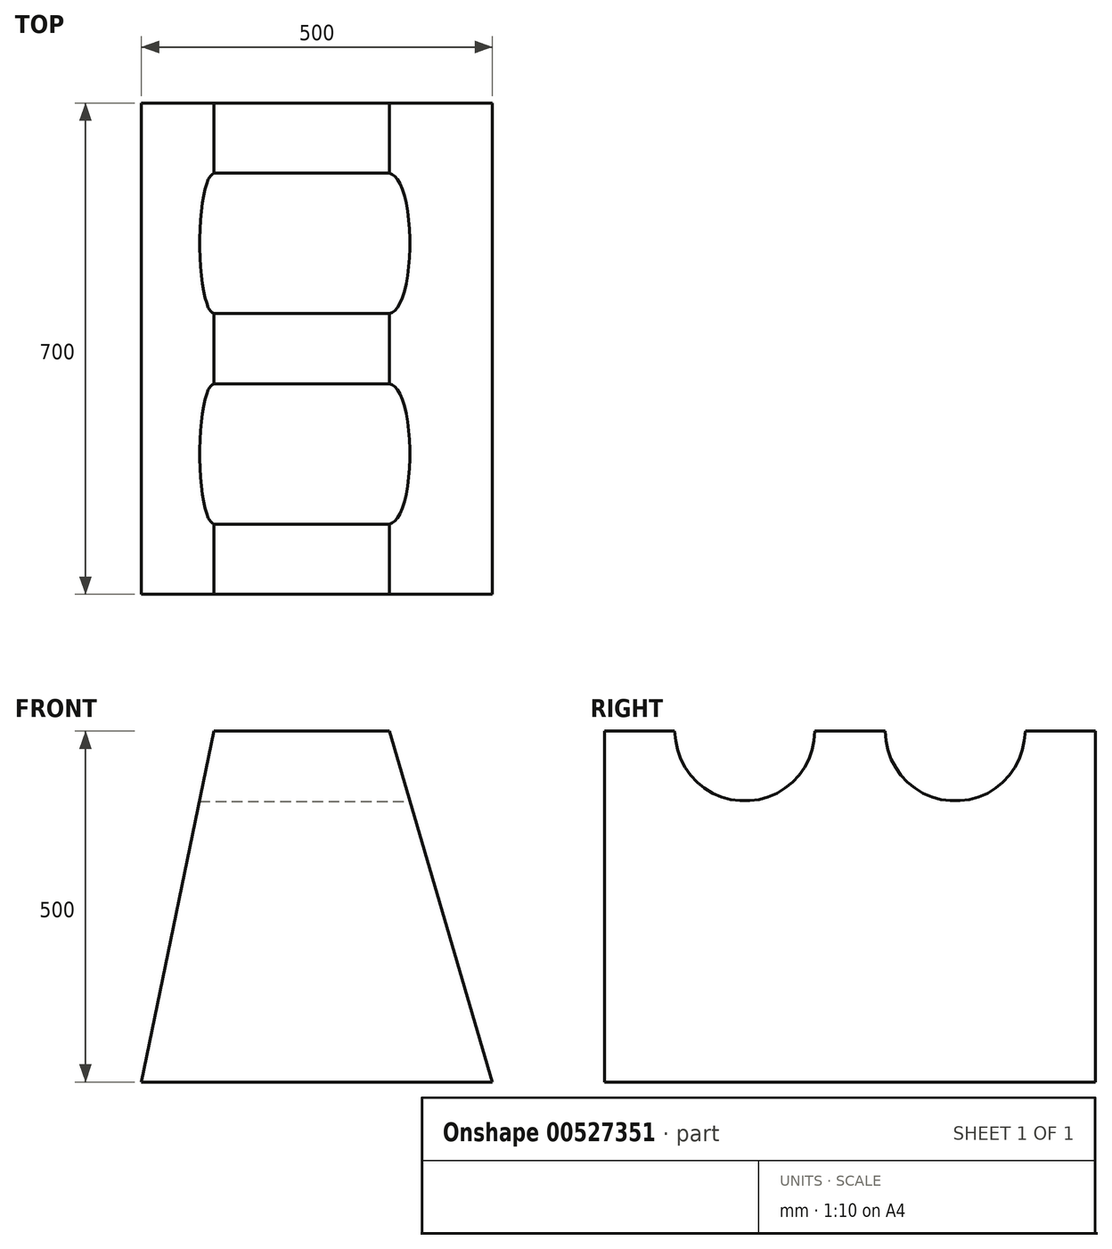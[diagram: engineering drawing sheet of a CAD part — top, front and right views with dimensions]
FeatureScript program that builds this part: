
annotation { "Feature Type Name" : "Feature", "Feature Type Description" : "" }
export const myFeature = defineFeature(function(context is Context, id is Id, definition is map)
    precondition{}
    {
        {
            var Q0;
            Q0=qCreatedBy(makeId("Front.planeOp"),FACE);
            var sketch = newSketch(context, id + "F0", { "sketchPlane" : qUnion([Q0])});
            skLineSegment(sketch, "E0", {"start": v(124.12, 332.38) * mm, "end": v(-125.88, 332.38) * mm});
            skLineSegment(sketch, "E1", {"start": v(-125.88, 332.38) * mm, "end": v(-229.3, -167.62) * mm});
            skLineSegment(sketch, "E2", {"start": v(-229.3, -167.62) * mm, "end": v(270.7, -167.62) * mm});
            skLineSegment(sketch, "E3", {"start": v(270.7, -167.62) * mm, "end": v(124.12, 332.38) * mm});
            skSolve(sketch);
        }
        {
            var Q0;
            Q0 = qSketchRegion(id + "F0", true);
            extrude(context, id + "F1", {"entities" : qUnion([Q0]), "oppositeDirection" : true, "depth" : 700 * mm, "offsetDistance" : 25 * mm});
        }
        {
            var Q0;
            Q0=qCreatedBy(makeId("Right.planeOp"),FACE);
            var sketch = newSketch(context, id + "F2", { "sketchPlane" : qUnion([Q0])});
            skCircle(sketch, "E4", {"center": v(200, 332.38) * mm, "radius": 100 * mm});
            skCircle(sketch, "E5", {"center": v(500, 332.38) * mm, "radius": 100 * mm});
            skSolve(sketch);
        }
        {
            var Q0;
            Q0 = qSketchRegion(id + "F2", true);
            extrude(context, id + "F3", {"entities" : qUnion([Q0]), "operationType" : NewBodyOperationType.REMOVE, "oppositeDirection" : true, "depth" : 400 * mm, "offsetDistance" : 25 * mm, "hasSecondDirection" : true, "secondDirectionOppositeDirection" : false, "secondDirectionDepth" : 310 * mm});
        }
    });
